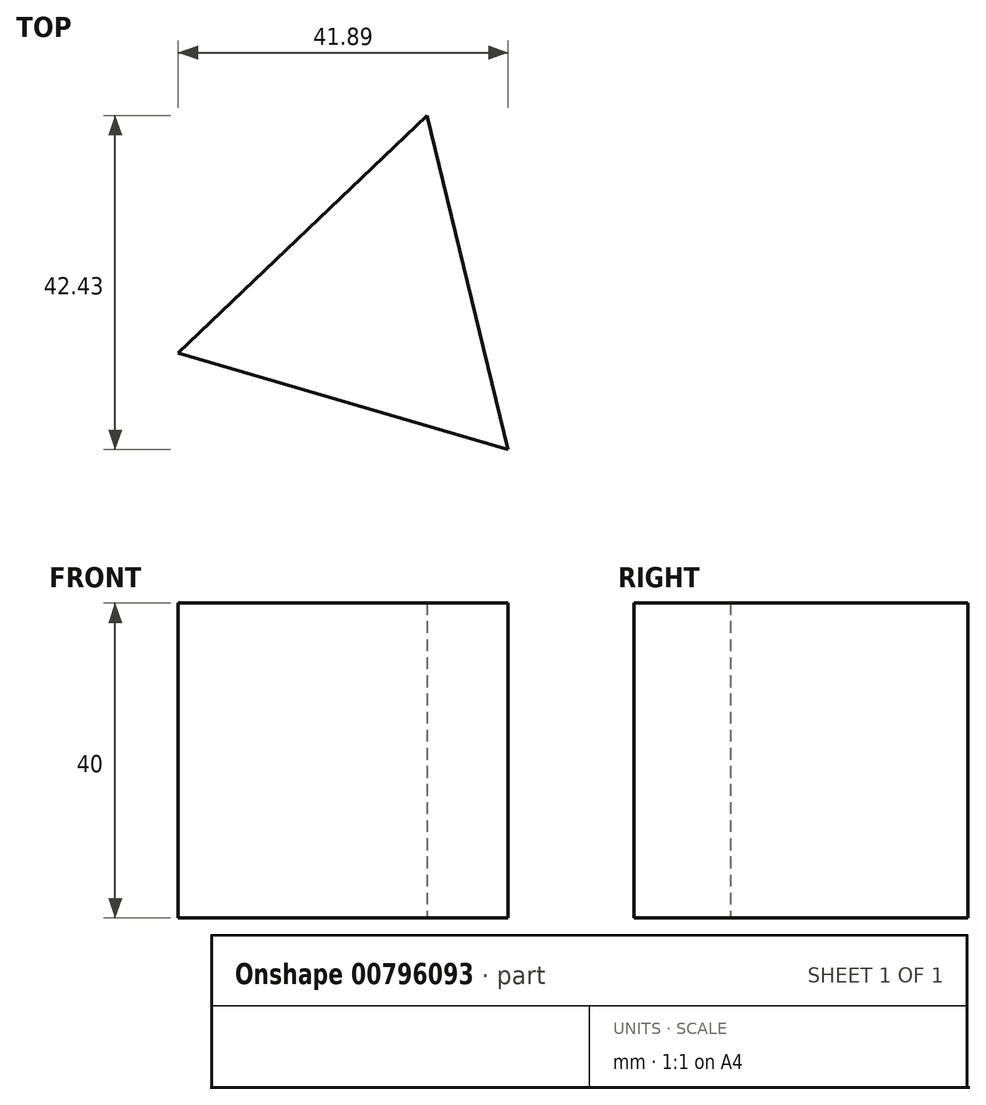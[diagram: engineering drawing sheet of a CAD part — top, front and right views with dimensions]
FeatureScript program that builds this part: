
annotation { "Feature Type Name" : "Feature", "Feature Type Description" : "" }
export const myFeature = defineFeature(function(context is Context, id is Id, definition is map)
    precondition{}
    {
        {
            var Q0;
            Q0=qCreatedBy(makeId("Top.planeOp"),FACE);
            var sketch = newSketch(context, id + "F0", { "sketchPlane" : qUnion([Q0])});
            skCircle(sketch, "E0.cCircle", {"center": v(-12.25, 13.85) * mm, "radius": 12.6 * mm, "construction": true});
            skLineSegment(sketch, "E0.0", {"start": v(-5.15, 38.04) * mm, "end": v(5.15, -4.39) * mm});
            skLineSegment(sketch, "E0.1", {"start": v(5.15, -4.39) * mm, "end": v(-36.74, 7.9) * mm});
            skLineSegment(sketch, "E0.2", {"start": v(-36.74, 7.9) * mm, "end": v(-5.15, 38.04) * mm});
            skPoint(sketch, "E0.0.midPoint", {"position": v(0, 16.83) * mm});
            skSolve(sketch);
        }
        {
            var Q0;
            Q0=makeQuery(id+"F0.imprint","IMPRINT",FACE,{"disambiguationData":[TD([[makeQuery(id+"F0.imprint","IMPRINT",EDGE,{"derivedFrom":sQuery(id+"F0.wireOp",EDGE,"E0.0")}),-1.0]])]});
            extrude(context, id + "F1", {"entities" : qUnion([Q0]), "depth" : 40 * mm, "offsetDistance" : 25 * mm});
        }
    });
